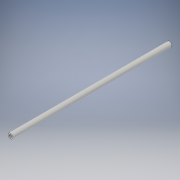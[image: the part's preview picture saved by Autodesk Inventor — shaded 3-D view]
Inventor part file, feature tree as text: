
AUTODESK INVENTOR PART (.ipt)
format: ipt  version: 2019.1 (Build 231200000, 200)  size: 99,840 bytes
history: native  units: in
note: dims shown in document units (in); Inventor stores cm internally (conversion verified against a paired STEP export)
features: sketch x2, extrude x1, hole x1, mirror x1
ambient origin geometry x8: Origin, YZ Plane, XZ Plane, XY Plane, X Axis, Y Axis, Z Axis, Center Point
bodies: Solid1 (feature_tree)
feature tree (5):
  extrude  "Extrusion1"  Depth=8.02in TaperAngle=0.0deg
  hole  "Hole1"  [1 undecoded]
  mirror  "Mirror1"
  sketch  "Sketch1"  dims[d0=0.25in d1=8.02in d2=0.0in]
  sketch  "Sketch2"  dims[d3=0.13in d4=0.328in d5=0.281in d6=0.138in d7=0.5635in d8=0.484in d9=0.8108in]
note: 1 required parameter value undecoded (feature->parameter linkage not recoverable at this tier; creation-order binding heuristic only, values carry confidence <= 0.55)
